# Revit family: Ladder_Incline-Ship_UPNOVR_U-504
name_source: partatom
category: Generic Models
units: mm (PartAtom-declared; Revit-internal decimal feet)

## family parameters
Always vertical = Yes
Can host rebar = No
Classification Number = 23.50.90.21
Cut with Voids When Loaded = No
Maintain Annotation Orientation = No
Part Type = Normal
Room Calculation Point = No
Round Connector Dimension = Use Diameter
Shared = No
Work Plane-Based = Yes

## types (1)
- As Specified
    Assembly Code = E1090900
    Capacity = 500 lbs per rung
    Cost = 0 $
    Default Elevation = 4' - 0"
    Description = UPNOVR U-504 Mezzanine Access with Platform Inclined Aluminum Ships Ladder
    Green Building-LEED = https://www.arcat.com
    Keynote = 05 51 33
    Manufacturer = UPNOVR, Inc.
    Model = U-504
    Product Data = http://www.arcat.com
    Standards Conformance = OSHA and ANSI A14.3
    URL = https://www.upnovr.com
    Unit Width = 2' - 0"
    Warranty Duration (Years) = 0

## geometry (parser evidence)
native form markers: Sweep x6
no freeform markers — native parametric forms only
